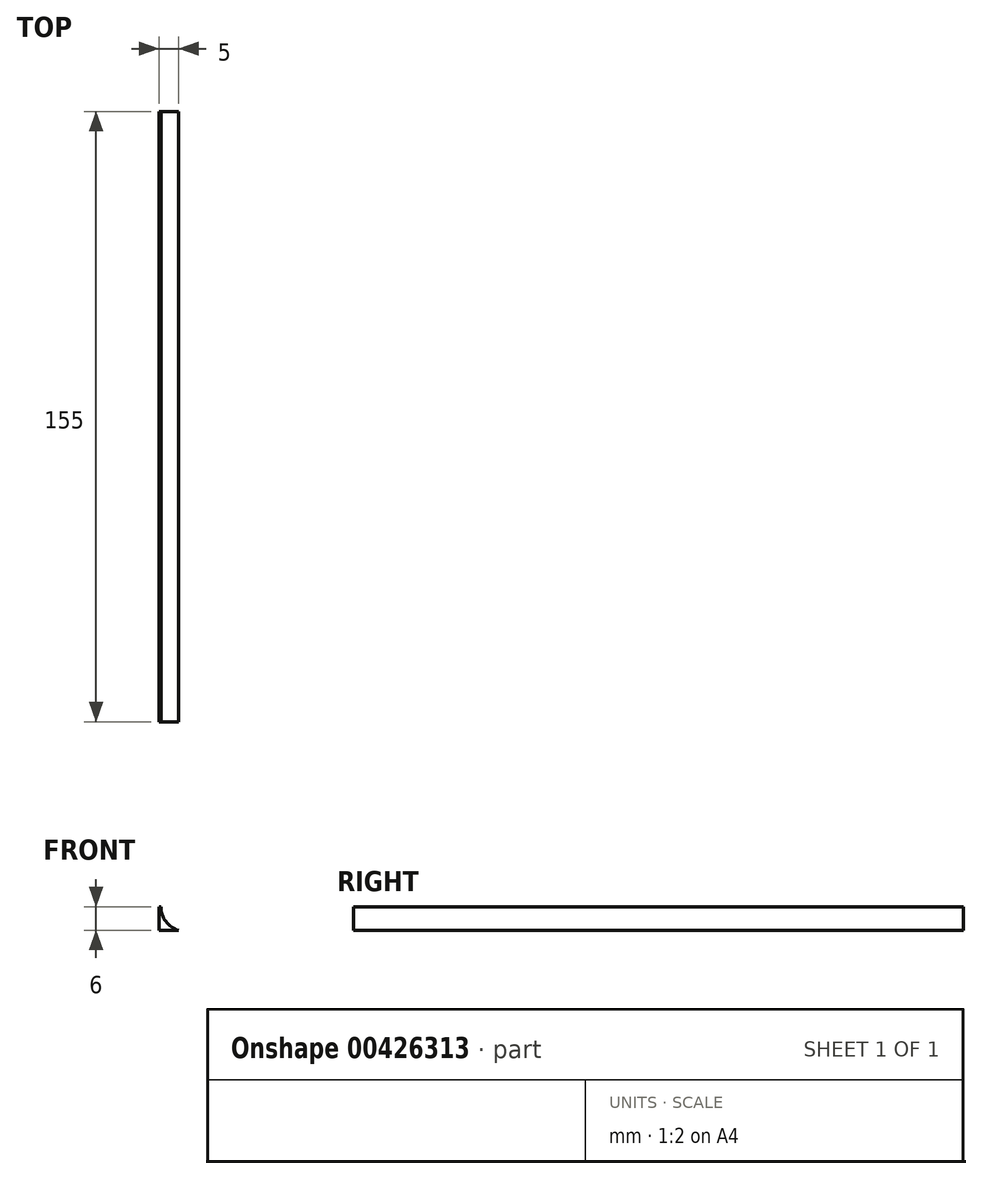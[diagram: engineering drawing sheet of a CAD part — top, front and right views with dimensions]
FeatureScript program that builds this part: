
annotation { "Feature Type Name" : "Feature", "Feature Type Description" : "" }
export const myFeature = defineFeature(function(context is Context, id is Id, definition is map)
    precondition{}
    {
        {
            var Q0;
            Q0=qCreatedBy(makeId("Front.planeOp"),FACE);
            var sketch = newSketch(context, id + "F0", { "sketchPlane" : qUnion([Q0])});
            skLineSegment(sketch, "E0.right", {"start": v(0, 0) * mm, "end": v(0, 6) * mm});
            skArc(sketch, "E1", {"start": v(0.5, 6) * mm, "mid": v(1.75, 2.25) * mm, "end": v(5, 0) * mm});
            skLineSegment(sketch, "E2", {"start": v(0, 6) * mm, "end": v(0.5, 6) * mm});
            skLineSegment(sketch, "E3", {"start": v(0, 0) * mm, "end": v(5, 0) * mm});
            skSolve(sketch);
        }
        {
            var Q0;
            Q0 = qSketchRegion(id + "F0", true);
            extrude(context, id + "F1", {"entities" : qUnion([Q0]), "depth" : 155 * mm, "offsetDistance" : 25 * mm});
        }
    });
